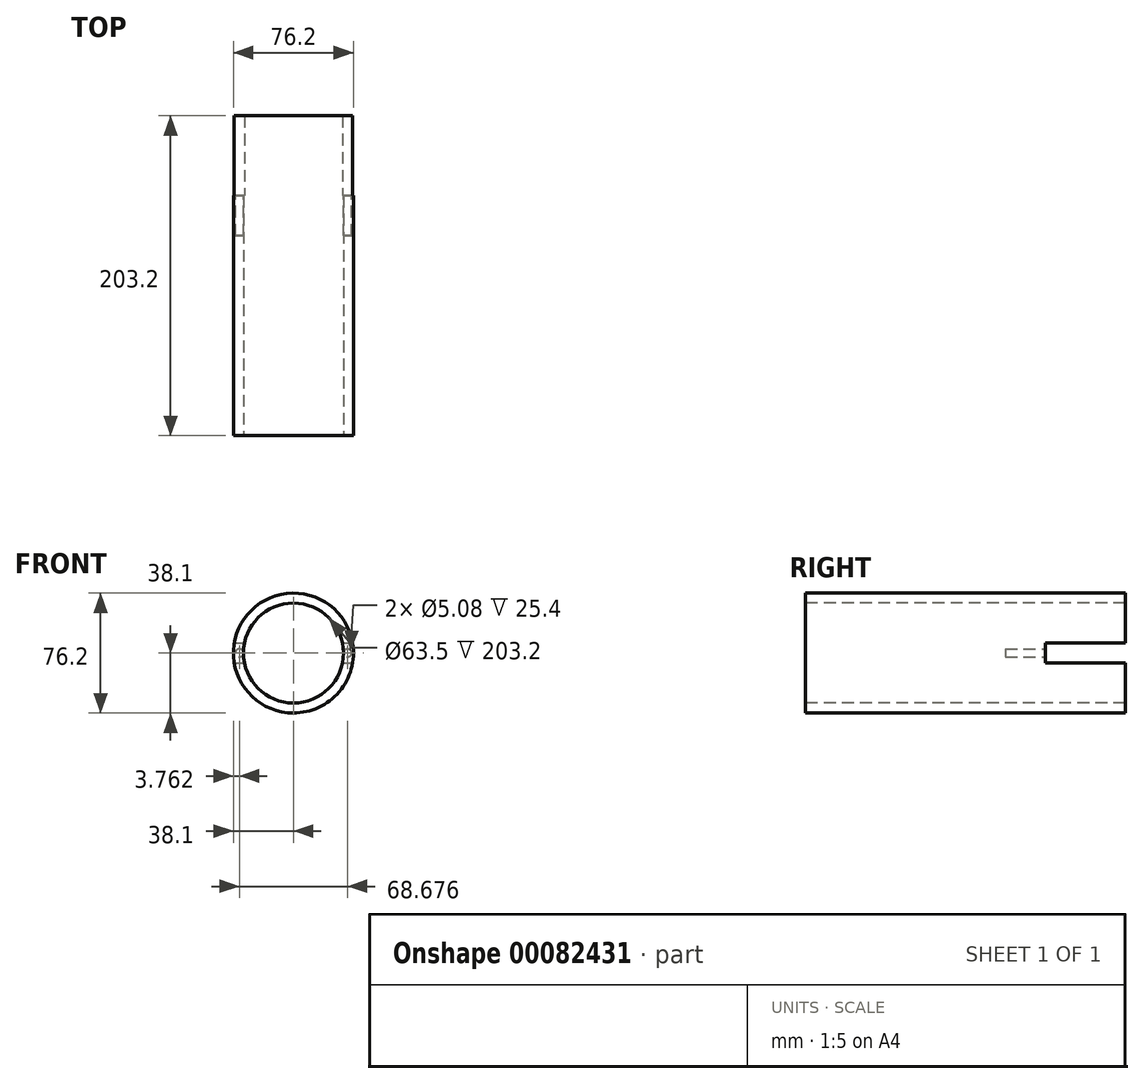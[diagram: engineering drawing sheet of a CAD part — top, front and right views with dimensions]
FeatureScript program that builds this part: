
annotation { "Feature Type Name" : "Feature", "Feature Type Description" : "" }
export const myFeature = defineFeature(function(context is Context, id is Id, definition is map)
    precondition{}
    {
        {
            var Q0;
            Q0=qCreatedBy(makeId("Front.planeOp"),FACE);
            var sketch = newSketch(context, id + "F0", { "sketchPlane" : qUnion([Q0])});
            skCircle(sketch, "E0", {"center": v(0, 0) * mm, "radius": 38.1 * mm});
            skSolve(sketch);
        }
        {
            var Q0;
            Q0 = qSketchRegion(id + "F0", true);
            extrude(context, id + "F1", {"entities" : qUnion([Q0]), "depth" : 203.2 * mm});
        }
        {
            var Q0;
            Q0=makeQuery(id+"F1.opExtrude","CAP_FACE",FACE,{"disambiguationData":[OSD([sQuery(id+"F0.wireOp",EDGE,"E0")])],"isStart":false});
            var sketch = newSketch(context, id + "F2", { "sketchPlane" : qUnion([Q0])});
            skCircle(sketch, "E1", {"center": v(0, 0) * mm, "radius": 31.75 * mm});
            skSolve(sketch);
        }
        {
            var Q0;
            Q0 = qSketchRegion(id + "F2", true);
            extrude(context, id + "F3", {"entities" : qUnion([Q0]), "operationType" : NewBodyOperationType.REMOVE, "oppositeDirection" : true, "depth" : 228.6 * mm});
        }
        {
            var Q0;
            Q0=qCreatedBy(makeId("Front.planeOp"),FACE);
            var sketch = newSketch(context, id + "F4", { "sketchPlane" : qUnion([Q0])});
            skLineSegment(sketch, "E2.bottom", {"start": v(-38.1, -6.35) * mm, "end": v(38.1, -6.35) * mm});
            skLineSegment(sketch, "E2.top", {"start": v(-38.1, 6.35) * mm, "end": v(38.1, 6.35) * mm});
            skLineSegment(sketch, "E2.left", {"start": v(-38.1, -6.35) * mm, "end": v(-38.1, 6.35) * mm});
            skLineSegment(sketch, "E2.right", {"start": v(38.1, -6.35) * mm, "end": v(38.1, 6.35) * mm});
            skPoint(sketch, "E2.middle", {"position": v(0, 0) * mm});
            skSolve(sketch);
        }
        {
            var Q0;
            Q0 = qSketchRegion(id + "F4", true);
            extrude(context, id + "F5", {"entities" : qUnion([Q0]), "operationType" : NewBodyOperationType.REMOVE, "depth" : 50.8 * mm});
        }
        {
            var Q0;
            Q0=makeQuery(id+"F5.boolean.opBoolean","COPY",FACE,{"disambiguationData":[OD(1.0)],"derivedFrom":makeQuery(id+"F5.opExtrude","CAP_FACE",FACE,{"disambiguationData":[OSD([sQuery(id+"F4.wireOp",EDGE,"E2.bottom"),sQuery(id+"F4.wireOp",EDGE,"E2.top"),sQuery(id+"F4.wireOp",EDGE,"E2.left"),sQuery(id+"F4.wireOp",EDGE,"E2.right")])],"isStart":false})});
            var sketch = newSketch(context, id + "F6", { "sketchPlane" : qUnion([Q0])});
            skCircle(sketch, "E3", {"center": v(-34.34, 0) * mm, "radius": 2.54 * mm});
            skPoint(sketch, "E3.centerSnap0", {"position": v(-38.1, 0) * mm});
            skPoint(sketch, "E3.centerSnap1", {"position": v(-34.34, 6.35) * mm});
            skLineSegment(sketch, "E4", {"start": v(0, 47.06) * mm, "end": v(0, -41.57) * mm, "construction": true});
            skCircle(sketch, "E5.MirrorC", {"center": v(34.34, 0) * mm, "radius": 2.54 * mm});
            skSolve(sketch);
        }
        {
            var Q0;
            Q0 = qSketchRegion(id + "F6", true);
            extrude(context, id + "F7", {"entities" : qUnion([Q0]), "operationType" : NewBodyOperationType.REMOVE, "oppositeDirection" : true, "depth" : 25.4 * mm});
        }
    });
